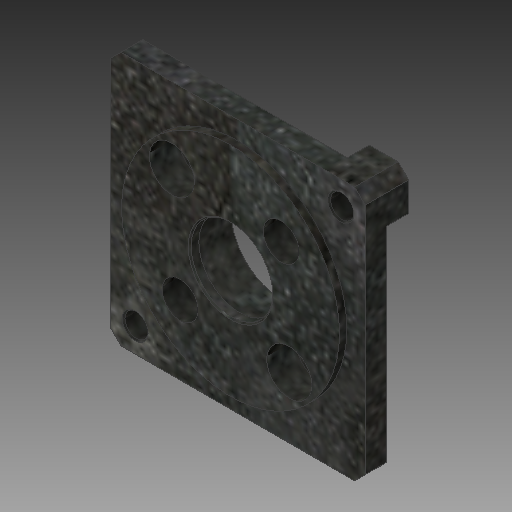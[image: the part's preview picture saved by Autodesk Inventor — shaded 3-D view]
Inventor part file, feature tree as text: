
AUTODESK INVENTOR PART (.ipt)
format: ipt  version: 2018 (Build 220112000, 112)  size: 298,496 bytes
history: native  units: in
note: dims shown in document units (in); Inventor stores cm internally (conversion verified against a paired STEP export)
features: chamfer x1
ambient origin geometry x8: Origin, YZ Plane, XZ Plane, XY Plane, X Axis, Y Axis, Z Axis, Center Point
bodies: Solid1 (feature_tree)
feature tree (1):
  chamfer  "Chamfer1"  [1 undecoded]
note: 1 required parameter value undecoded (feature->parameter linkage not recoverable at this tier; creation-order binding heuristic only, values carry confidence <= 0.55)
